# Revit family: EURS_63_LF_FB_BY121 PSU
name_source: partatom
category: Lighting Fixtures
revit_build: Autodesk Revit 2018 (Build: 20190510_1515(x64)
units: mm (PartAtom-declared; Revit-internal decimal feet)

## family parameters
Cut with Voids When Loaded = No
Host = Face
Light Source = No
Part Type = Normal
Room Calculation Point = No
Round Connector Dimension = Use Diameter
Shared = Yes

## types (1)
- EURS_63_LF_FB_BY121 PSU
    Apparent Load = 0 VA
    BIM Library - URL = http://www.lighting.philips.com
    Content modified date = 08-03-2021
    Content version = 1.0
    Default Elevation = 0 mm  [stored 0 ft]
    Description = Coreline Highbay Gen4 BY121 PSU
    Height = 95 mm
    Lamp = LAMP TYPE
    Lamp type = BY121P IES Data : G4 PSU 1 xLED200S_840 NB
    Last IES update = 08-03-2021
    Length = 450 mm  [stored 1.47638 ft]
    Light source = 2 mm  [stored 0.00656168 ft]
    Manufacturer = Philips
    Model = BY121
    Product catalog - URL = https://www.lighting.philips.com
    Type Comments = Face Based
    URL = http://www.lighting.philips.com
    Voltage (V) = 230 V
    Width = 450 mm  [stored 1.47638 ft]

note: [stored X ft] marks values corroborated as IEEE doubles in the binary element streams (Revit-internal decimal feet)

## geometry (parser evidence)
native form markers: Sweep x12
no freeform markers — native parametric forms only
